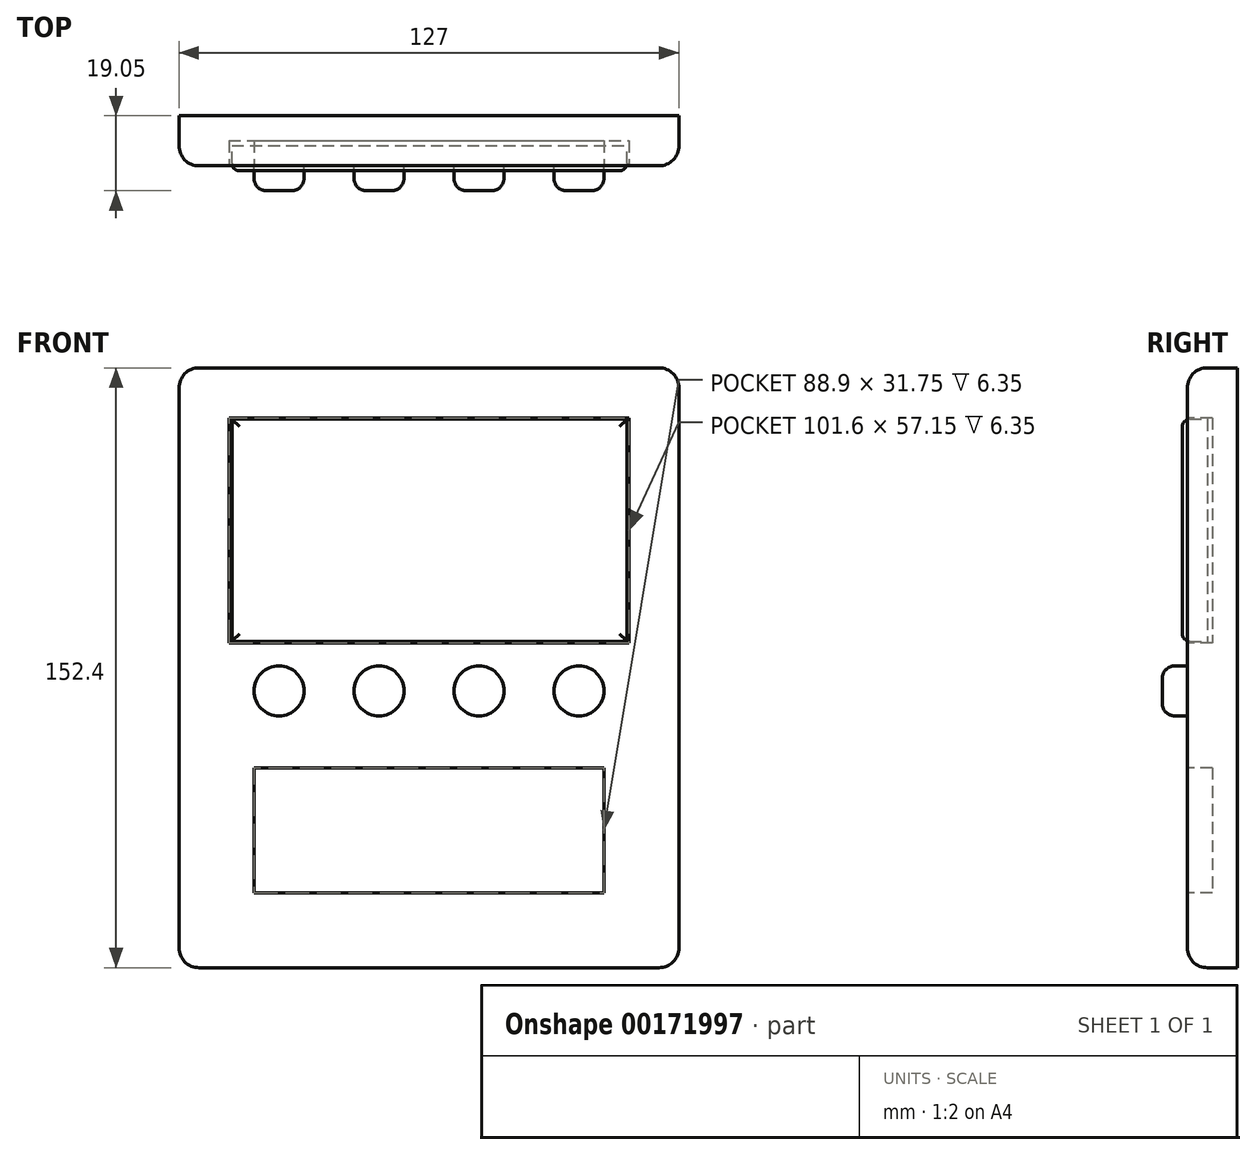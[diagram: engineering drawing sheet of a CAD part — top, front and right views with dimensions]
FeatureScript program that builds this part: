
annotation { "Feature Type Name" : "Feature", "Feature Type Description" : "" }
export const myFeature = defineFeature(function(context is Context, id is Id, definition is map)
    precondition{}
    {
        {
            var Q0;
            Q0=qCreatedBy(makeId("Front.planeOp"),FACE);
            var sketch = newSketch(context, id + "F0", { "sketchPlane" : qUnion([Q0])});
            skLineSegment(sketch, "E0.bottom", {"start": v(63.5, 76.2) * mm, "end": v(-63.5, 76.2) * mm});
            skLineSegment(sketch, "E0.top", {"start": v(63.5, -76.2) * mm, "end": v(-63.5, -76.2) * mm});
            skLineSegment(sketch, "E0.left", {"start": v(63.5, 76.2) * mm, "end": v(63.5, -76.2) * mm});
            skLineSegment(sketch, "E0.right", {"start": v(-63.5, 76.2) * mm, "end": v(-63.5, -76.2) * mm});
            skPoint(sketch, "E0.middle", {"position": v(0, 0) * mm});
            skSolve(sketch);
        }
        {
            var Q0;
            Q0=qSketchRegion(id+"F0",true);
            extrude(context, id + "F1", {"entities" : qUnion([Q0]), "oppositeDirection" : true, "depth" : 12.7 * mm});
        }
        {
            var Q0;
            Q0=makeQuery(id+"F1.opExtrude","CAP_FACE",FACE,{"disambiguationData":[OSD([sQuery(id+"F0.wireOp",EDGE,"E0.bottom"),sQuery(id+"F0.wireOp",EDGE,"E0.top"),sQuery(id+"F0.wireOp",EDGE,"E0.left"),sQuery(id+"F0.wireOp",EDGE,"E0.right")])],"isStart":true});
            var sketch = newSketch(context, id + "F2", { "sketchPlane" : qUnion([Q0])});
            skLineSegment(sketch, "E1.bottom", {"start": v(-50.8, 63.5) * mm, "end": v(50.8, 63.5) * mm});
            skLineSegment(sketch, "E1.top", {"start": v(-50.8, 6.35) * mm, "end": v(50.8, 6.35) * mm});
            skLineSegment(sketch, "E1.left", {"start": v(-50.8, 63.5) * mm, "end": v(-50.8, 6.35) * mm});
            skLineSegment(sketch, "E1.right", {"start": v(50.8, 63.5) * mm, "end": v(50.8, 6.35) * mm});
            skCircle(sketch, "E2", {"center": v(-38.1, -5.87) * mm, "radius": 6.35 * mm});
            skCircle(sketch, "E3", {"center": v(-12.7, -5.87) * mm, "radius": 6.35 * mm});
            skCircle(sketch, "E4", {"center": v(12.7, -5.87) * mm, "radius": 6.35 * mm});
            skCircle(sketch, "E5", {"center": v(38.1, -5.87) * mm, "radius": 6.35 * mm});
            skLineSegment(sketch, "E6.bottom", {"start": v(-44.45, -25.4) * mm, "end": v(44.45, -25.4) * mm});
            skLineSegment(sketch, "E6.top", {"start": v(-44.45, -57.15) * mm, "end": v(44.45, -57.15) * mm});
            skLineSegment(sketch, "E6.left", {"start": v(-44.45, -25.4) * mm, "end": v(-44.45, -57.15) * mm});
            skLineSegment(sketch, "E6.right", {"start": v(44.45, -25.4) * mm, "end": v(44.45, -57.15) * mm});
            skSolve(sketch);
        }
        {
            var Q0;
            Q0=makeQuery(id+"F2.imprint","IMPRINT",FACE,{"disambiguationData":[TD([[makeQuery(id+"F2.imprint","IMPRINT",EDGE,{"derivedFrom":sQuery(id+"F2.wireOp",EDGE,"E1.bottom")}),-1.0]])]});
            var Q1;
            Q1=makeQuery(id+"F2.imprint","IMPRINT",FACE,{"disambiguationData":[TD([[makeQuery(id+"F2.imprint","IMPRINT",EDGE,{"derivedFrom":sQuery(id+"F2.wireOp",EDGE,"E6.bottom")}),-1.0]])]});
            extrude(context, id + "F3", {"entities" : qUnion([Q0, Q1]), "operationType" : NewBodyOperationType.REMOVE, "oppositeDirection" : true, "depth" : 6.35 * mm});
        }
        {
            var Q0;
            Q0=makeQuery(id+"F2.imprint","IMPRINT",FACE,{"disambiguationData":[TD([[makeQuery(id+"F2.imprint","IMPRINT",EDGE,{"derivedFrom":sQuery(id+"F2.wireOp",EDGE,"E2")}),1.0]])]});
            var Q1;
            Q1=makeQuery(id+"F2.imprint","IMPRINT",FACE,{"disambiguationData":[TD([[makeQuery(id+"F2.imprint","IMPRINT",EDGE,{"derivedFrom":sQuery(id+"F2.wireOp",EDGE,"E3")}),1.0]])]});
            var Q2;
            Q2=makeQuery(id+"F2.imprint","IMPRINT",FACE,{"disambiguationData":[TD([[makeQuery(id+"F2.imprint","IMPRINT",EDGE,{"derivedFrom":sQuery(id+"F2.wireOp",EDGE,"E4")}),1.0]])]});
            var Q3;
            Q3=makeQuery(id+"F2.imprint","IMPRINT",FACE,{"disambiguationData":[TD([[makeQuery(id+"F2.imprint","IMPRINT",EDGE,{"derivedFrom":sQuery(id+"F2.wireOp",EDGE,"E5")}),1.0]])]});
            var Q4;
            Q4=sQuery(id+"F2.wireOp",EDGE,"E2");
            var Q5;
            Q5=sQuery(id+"F2.wireOp",EDGE,"E3");
            var Q6;
            Q6=sQuery(id+"F2.wireOp",EDGE,"E4");
            var Q7;
            Q7=sQuery(id+"F2.wireOp",EDGE,"E5");
            extrude(context, id + "F4", {"entities" : qUnion([Q0, Q1, Q2, Q3]), "surfaceEntities" : qUnion([Q4, Q5, Q6, Q7]), "depth" : 6.35 * mm});
        }
        {
            var Q0;
            Q0=makeQuery(id+"F2.imprint","IMPRINT",FACE,{"disambiguationData":[TD([[makeQuery(id+"F2.imprint","IMPRINT",EDGE,{"derivedFrom":sQuery(id+"F2.wireOp",EDGE,"E1.bottom")}),1.0]])]});
            cPlane(context, id + "F5", {"entities" : qUnion([Q0]), "cplaneType" : CPlaneType.OFFSET, "offset" : 5.08 * mm, "oppositeDirection" : true, "width" : 152.4 * mm, "height" : 152.4 * mm});
        }
        {
            var Q0;
            Q0=qCreatedBy(id+"F5.planeOp",FACE);
            var sketch = newSketch(context, id + "F6", { "sketchPlane" : qUnion([Q0])});
            skLineSegment(sketch, "E7.bottom", {"start": v(-50.05, 63.16) * mm, "end": v(50.3, 63.16) * mm});
            skLineSegment(sketch, "E7.top", {"start": v(-50.05, 6.75) * mm, "end": v(50.3, 6.75) * mm});
            skLineSegment(sketch, "E7.left", {"start": v(-50.05, 63.16) * mm, "end": v(-50.05, 6.75) * mm});
            skLineSegment(sketch, "E7.right", {"start": v(50.3, 63.16) * mm, "end": v(50.3, 6.75) * mm});
            skSolve(sketch);
        }
        {
            var Q0;
            Q0=qSketchRegion(id+"F6",true);
            extrude(context, id + "F7", {"entities" : qUnion([Q0]), "depth" : 6.35 * mm});
        }
        {
            var Q0;
            Q0=makeQuery(id+"F4.opExtrude","CAP_EDGE",EDGE,{"disambiguationData":[OSD([sQuery(id+"F2.wireOp",EDGE,"E2")])],"isStart":false});
            var Q1;
            Q1=makeQuery(id+"F4.opExtrude","CAP_EDGE",EDGE,{"disambiguationData":[OSD([sQuery(id+"F2.wireOp",EDGE,"E3")])],"isStart":false});
            var Q2;
            Q2=makeQuery(id+"F4.opExtrude","CAP_EDGE",EDGE,{"disambiguationData":[OSD([sQuery(id+"F2.wireOp",EDGE,"E4")])],"isStart":false});
            var Q3;
            Q3=makeQuery(id+"F4.opExtrude","CAP_EDGE",EDGE,{"disambiguationData":[OSD([sQuery(id+"F2.wireOp",EDGE,"E5")])],"isStart":false});
            fillet(context, id + "F8", {"entities" : qUnion([Q0, Q1, Q2, Q3]), "radius" : 3.17 * mm, "tangentPropagation" : true, "allowEdgeOverflow" : false});
        }
        {
            var Q0;
            Q0=makeQuery(id+"F7.opExtrude","CAP_EDGE",EDGE,{"disambiguationData":[OSD([sQuery(id+"F6.wireOp",EDGE,"E7.left")])],"isStart":false});
            var Q1;
            Q1=makeQuery(id+"F7.opExtrude","CAP_EDGE",EDGE,{"disambiguationData":[OSD([sQuery(id+"F6.wireOp",EDGE,"E7.bottom")])],"isStart":false});
            var Q2;
            Q2=makeQuery(id+"F7.opExtrude","CAP_EDGE",EDGE,{"disambiguationData":[OSD([sQuery(id+"F6.wireOp",EDGE,"E7.top")])],"isStart":false});
            var Q3;
            Q3=makeQuery(id+"F7.opExtrude","CAP_EDGE",EDGE,{"disambiguationData":[OSD([sQuery(id+"F6.wireOp",EDGE,"E7.right")])],"isStart":false});
            fillet(context, id + "F9", {"entities" : qUnion([Q0, Q1, Q2, Q3]), "radius" : 1.9 * mm, "tangentPropagation" : true, "allowEdgeOverflow" : false});
        }
        {
            var Q0;
            Q0=makeQuery(id+"F1.opExtrude","SWEPT_EDGE",EDGE,{"disambiguationData":[OSD([sQuery(id+"F0.wireOp",EDGE,"E0.bottom"),sQuery(id+"F0.wireOp",EDGE,"E0.right")])]});
            var Q1;
            Q1=makeQuery(id+"F1.opExtrude","SWEPT_EDGE",EDGE,{"disambiguationData":[OSD([sQuery(id+"F0.wireOp",EDGE,"E0.bottom"),sQuery(id+"F0.wireOp",EDGE,"E0.left")])]});
            var Q2;
            Q2=makeQuery(id+"F1.opExtrude","SWEPT_EDGE",EDGE,{"disambiguationData":[OSD([sQuery(id+"F0.wireOp",EDGE,"E0.top"),sQuery(id+"F0.wireOp",EDGE,"E0.left")])]});
            var Q3;
            Q3=makeQuery(id+"F1.opExtrude","SWEPT_EDGE",EDGE,{"disambiguationData":[OSD([sQuery(id+"F0.wireOp",EDGE,"E0.top"),sQuery(id+"F0.wireOp",EDGE,"E0.right")])]});
            var Q4;
            Q4=makeQuery(id+"F1.opExtrude","CAP_EDGE",EDGE,{"disambiguationData":[OSD([sQuery(id+"F0.wireOp",EDGE,"E0.top")])],"isStart":true});
            var Q5;
            Q5=makeQuery(id+"F1.opExtrude","CAP_EDGE",EDGE,{"disambiguationData":[OSD([sQuery(id+"F0.wireOp",EDGE,"E0.right")])],"isStart":true});
            var Q6;
            Q6=makeQuery(id+"F1.opExtrude","CAP_EDGE",EDGE,{"disambiguationData":[OSD([sQuery(id+"F0.wireOp",EDGE,"E0.left")])],"isStart":true});
            var Q7;
            Q7=makeQuery(id+"F1.opExtrude","CAP_EDGE",EDGE,{"disambiguationData":[OSD([sQuery(id+"F0.wireOp",EDGE,"E0.bottom")])],"isStart":true});
            fillet(context, id + "F10", {"entities" : qUnion([Q0, Q1, Q2, Q3, Q4, Q5, Q6, Q7]), "radius" : 5.08 * mm, "tangentPropagation" : true, "allowEdgeOverflow" : false});
        }
    });
